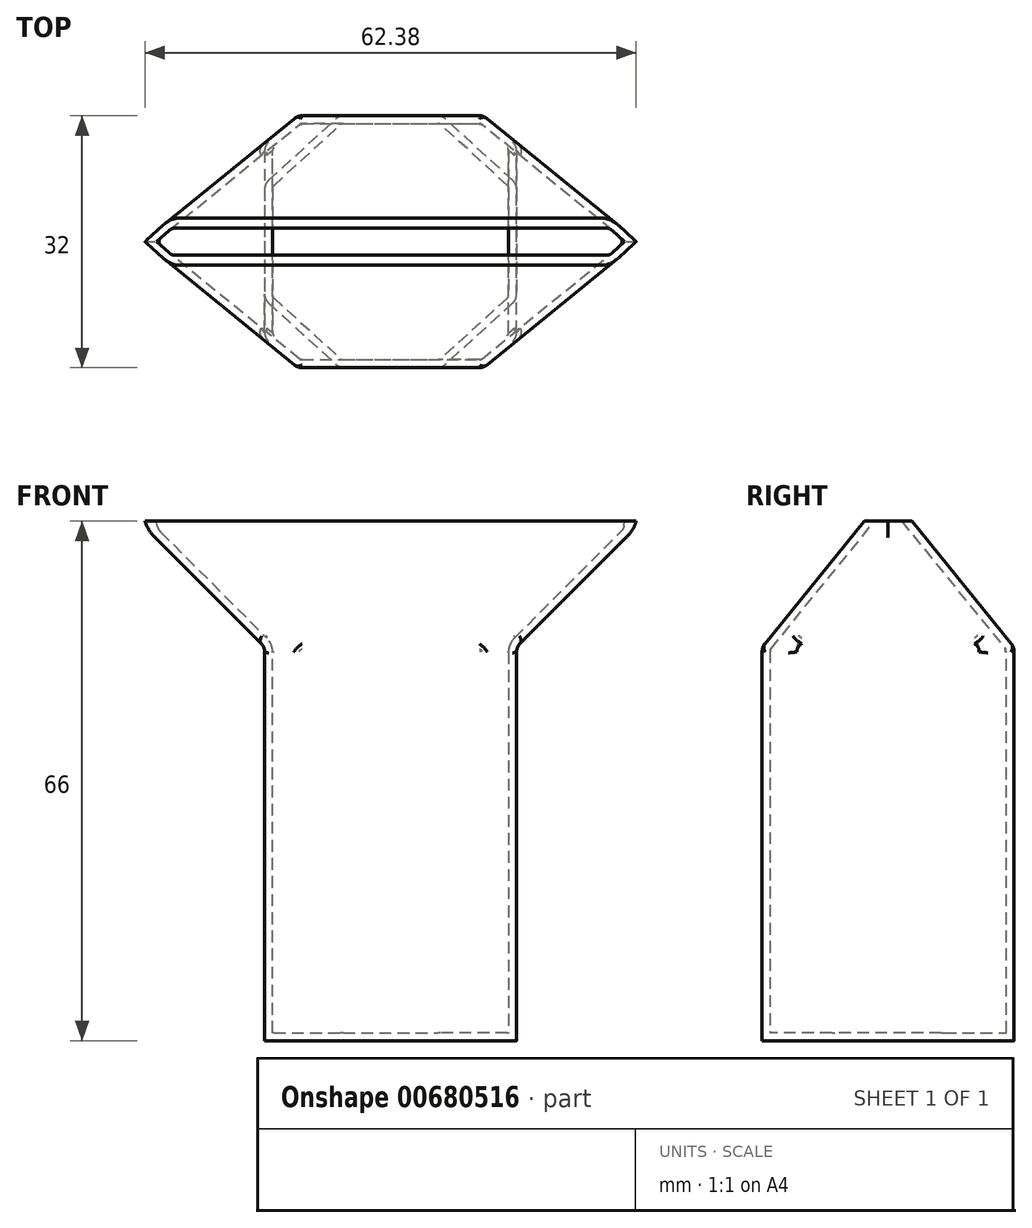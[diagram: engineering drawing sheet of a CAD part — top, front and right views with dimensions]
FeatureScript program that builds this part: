
annotation { "Feature Type Name" : "Feature", "Feature Type Description" : "" }
export const myFeature = defineFeature(function(context is Context, id is Id, definition is map)
    precondition{}
    {
        {
            assignVariable(context, id + "F0", {"name" : "length", "anyValue" : 32});
        }
        {
            assignVariable(context, id + "F1", {"name" : "depth", "anyValue" : 50});
        }
        {
            var Q0;
            Q0=qCreatedBy(makeId("Top.planeOp"),FACE);
            var sketch = newSketch(context, id + "F2", { "sketchPlane" : qUnion([Q0])});
            skLineSegment(sketch, "E0.bottom", {"start": v(-16, 16) * mm, "end": v(16, 16) * mm});
            skLineSegment(sketch, "E0.top", {"start": v(-16, -16) * mm, "end": v(16, -16) * mm});
            skLineSegment(sketch, "E0.left", {"start": v(-16, 16) * mm, "end": v(-16, -16) * mm});
            skLineSegment(sketch, "E0.right", {"start": v(16, 16) * mm, "end": v(16, -16) * mm});
            skPoint(sketch, "E0.middle", {"position": v(0, 0) * mm});
            skSolve(sketch);
        }
        {
            var Q0;
            Q0=qSketchRegion(id+"F2",true);
            extrude(context, id + "F3", {"entities" : qUnion([Q0]), "depth" : (getVariable(context, 'depth')) * mm, "offsetDistance" : 25 * mm});
        }
        {
            var Q0;
            Q0=makeQuery(id+"F3.opExtrude","CAP_FACE",FACE,{"disambiguationData":[OSD([sQuery(id+"F2.wireOp",EDGE,"E0.bottom"),sQuery(id+"F2.wireOp",EDGE,"E0.top"),sQuery(id+"F2.wireOp",EDGE,"E0.left"),sQuery(id+"F2.wireOp",EDGE,"E0.right")])],"isStart":false});
            cPlane(context, id + "F4", {"entities" : qUnion([Q0]), "cplaneType" : CPlaneType.OFFSET, "offset" : (getVariable(context, 'length') / 2) * mm, "width" : 150 * mm, "height" : 150 * mm});
        }
        {
            var Q0;
            Q0=qCreatedBy(id+"F4.planeOp",FACE);
            var sketch = newSketch(context, id + "F5", { "sketchPlane" : qUnion([Q0])});
            skLineSegment(sketch, "E1.bottom", {"start": v(32, 3) * mm, "end": v(-32, 3) * mm});
            skLineSegment(sketch, "E1.top", {"start": v(32, -3) * mm, "end": v(-32, -3) * mm});
            skLineSegment(sketch, "E1.left", {"start": v(32, 3) * mm, "end": v(32, -3) * mm});
            skLineSegment(sketch, "E1.right", {"start": v(-32, 3) * mm, "end": v(-32, -3) * mm});
            skPoint(sketch, "E1.middle", {"position": v(0, 0) * mm});
            skSolve(sketch);
        }
        {
            var Q1;
            Q1=makeQuery(id+"F3.opExtrude","CAP_FACE",FACE,{"disambiguationData":[OSD([sQuery(id+"F2.wireOp",EDGE,"E0.bottom"),sQuery(id+"F2.wireOp",EDGE,"E0.top"),sQuery(id+"F2.wireOp",EDGE,"E0.left"),sQuery(id+"F2.wireOp",EDGE,"E0.right")])],"isStart":false});
            var Q2;
            Q2=makeQuery(id+"F5.imprint","IMPRINT",FACE,{"disambiguationData":[TD([[makeQuery(id+"F5.imprint","IMPRINT",EDGE,{"derivedFrom":sQuery(id+"F5.wireOp",EDGE,"E1.bottom")}),1.0]])]});
            loft(context, id + "F6", {"operationType" : NewBodyOperationType.ADD, "sheetProfilesArray" : [{ "sheetProfileEntities" : qUnion([Q1]) }, { "sheetProfileEntities" : qUnion([Q2]) }]});
        }
        {
            var Q0;
            Q0=makeQuery(id+"F6.opLoft","SWEPT_EDGE",EDGE,{"disambiguationData":[OSD([sQuery(id+"F2.wireOp",EDGE,"E0.top"),sQuery(id+"F2.wireOp",EDGE,"E0.left"),sQuery(id+"F5.wireOp",EDGE,"E1.top"),sQuery(id+"F5.wireOp",EDGE,"E1.right")])]});
            var Q1;
            Q1=makeQuery(id+"F6.opLoft","SWEPT_EDGE",EDGE,{"disambiguationData":[OSD([sQuery(id+"F2.wireOp",EDGE,"E0.bottom"),sQuery(id+"F2.wireOp",EDGE,"E0.left"),sQuery(id+"F5.wireOp",EDGE,"E1.bottom"),sQuery(id+"F5.wireOp",EDGE,"E1.right")])]});
            var Q2;
            Q2=makeQuery(id+"F6.opLoft","SWEPT_EDGE",EDGE,{"disambiguationData":[OSD([sQuery(id+"F2.wireOp",EDGE,"E0.top"),sQuery(id+"F2.wireOp",EDGE,"E0.right"),sQuery(id+"F5.wireOp",EDGE,"E1.top"),sQuery(id+"F5.wireOp",EDGE,"E1.left")])]});
            var Q3;
            Q3=makeQuery(id+"F6.opLoft","SWEPT_EDGE",EDGE,{"disambiguationData":[OSD([sQuery(id+"F2.wireOp",EDGE,"E0.bottom"),sQuery(id+"F2.wireOp",EDGE,"E0.right"),sQuery(id+"F5.wireOp",EDGE,"E1.bottom"),sQuery(id+"F5.wireOp",EDGE,"E1.left")])]});
            chamfer(context, id + "F7", {"entities" : qUnion([Q0, Q1, Q2, Q3]), "width" : 2 * mm, "tangentPropagation" : true});
        }
        {
            var Q0;
            {var subQ0=sQuery(id+"F2.wireOp",EDGE,"E0.top");Q0=makeQuery(id+"F7.opChamfer","BLEND_EDGE",EDGE,{"blendedFrom":[makeQuery(id+"F6.opLoft","SWEPT_EDGE",EDGE,{"disambiguationData":[OSD([subQ0,sQuery(id+"F2.wireOp",EDGE,"E0.left"),sQuery(id+"F5.wireOp",EDGE,"E1.top"),sQuery(id+"F5.wireOp",EDGE,"E1.right")])]}),makeQuery(id+"F3.opExtrude","SWEPT_FACE",FACE,{"disambiguationData":[OSD([subQ0])]})],"blendedInto":[makeQuery(id+"F3.opExtrude","SWEPT_FACE",FACE,{"disambiguationData":[OSD([subQ0])]})]});}
            var Q1;
            {var subQ0=sQuery(id+"F2.wireOp",EDGE,"E0.left");Q1=makeQuery(id+"F7.opChamfer","BLEND_EDGE",EDGE,{"blendedFrom":[makeQuery(id+"F6.opLoft","SWEPT_EDGE",EDGE,{"disambiguationData":[OSD([sQuery(id+"F2.wireOp",EDGE,"E0.top"),subQ0,sQuery(id+"F5.wireOp",EDGE,"E1.top"),sQuery(id+"F5.wireOp",EDGE,"E1.right")])]}),makeQuery(id+"F3.opExtrude","SWEPT_FACE",FACE,{"disambiguationData":[OSD([subQ0])]})],"blendedInto":[makeQuery(id+"F3.opExtrude","SWEPT_FACE",FACE,{"disambiguationData":[OSD([subQ0])]})]});}
            var Q2;
            {var subQ0=sQuery(id+"F5.wireOp",EDGE,"E1.right");var subQ1=sQuery(id+"F5.wireOp",EDGE,"E1.top");var subQ2=sQuery(id+"F2.wireOp",EDGE,"E0.left");var subQ3=sQuery(id+"F2.wireOp",EDGE,"E0.top");Q2=makeQuery(id+"F7.opChamfer","BLEND_EDGE",EDGE,{"blendedFrom":[makeQuery(id+"F6.opLoft","SWEPT_EDGE",EDGE,{"disambiguationData":[OSD([subQ3,subQ2,subQ1,subQ0])]}),makeQuery(id+"F6.opLoft","SWEPT_FACE",FACE,{"disambiguationData":[OSD([sQuery(id+"F2.wireOp",EDGE,"E0.bottom"),subQ3,subQ2,sQuery(id+"F5.wireOp",EDGE,"E1.bottom"),subQ1,subQ0])]})],"blendedInto":[makeQuery(id+"F6.opLoft","SWEPT_FACE",FACE,{"disambiguationData":[OSD([sQuery(id+"F2.wireOp",EDGE,"E0.bottom"),subQ3,subQ2,sQuery(id+"F5.wireOp",EDGE,"E1.bottom"),subQ1,subQ0])]})]});}
            var Q3;
            {var subQ0=sQuery(id+"F5.wireOp",EDGE,"E1.right");var subQ1=sQuery(id+"F5.wireOp",EDGE,"E1.top");var subQ2=sQuery(id+"F2.wireOp",EDGE,"E0.left");var subQ3=sQuery(id+"F2.wireOp",EDGE,"E0.top");Q3=makeQuery(id+"F7.opChamfer","BLEND_EDGE",EDGE,{"blendedFrom":[makeQuery(id+"F6.opLoft","SWEPT_EDGE",EDGE,{"disambiguationData":[OSD([subQ3,subQ2,subQ1,subQ0])]}),makeQuery(id+"F6.opLoft","SWEPT_FACE",FACE,{"disambiguationData":[OSD([subQ3,subQ2,sQuery(id+"F2.wireOp",EDGE,"E0.right"),subQ1,sQuery(id+"F5.wireOp",EDGE,"E1.left"),subQ0])]})],"blendedInto":[makeQuery(id+"F6.opLoft","SWEPT_FACE",FACE,{"disambiguationData":[OSD([subQ3,subQ2,sQuery(id+"F2.wireOp",EDGE,"E0.right"),subQ1,sQuery(id+"F5.wireOp",EDGE,"E1.left"),subQ0])]})]});}
            var Q4;
            {var subQ0=sQuery(id+"F5.wireOp",EDGE,"E1.right");var subQ1=sQuery(id+"F5.wireOp",EDGE,"E1.bottom");var subQ2=sQuery(id+"F2.wireOp",EDGE,"E0.left");var subQ3=sQuery(id+"F2.wireOp",EDGE,"E0.bottom");Q4=makeQuery(id+"F7.opChamfer","BLEND_EDGE",EDGE,{"blendedFrom":[makeQuery(id+"F6.opLoft","SWEPT_EDGE",EDGE,{"disambiguationData":[OSD([subQ3,subQ2,subQ1,subQ0])]}),makeQuery(id+"F6.opLoft","SWEPT_FACE",FACE,{"disambiguationData":[OSD([subQ3,sQuery(id+"F2.wireOp",EDGE,"E0.top"),subQ2,subQ1,sQuery(id+"F5.wireOp",EDGE,"E1.top"),subQ0])]})],"blendedInto":[makeQuery(id+"F6.opLoft","SWEPT_FACE",FACE,{"disambiguationData":[OSD([subQ3,sQuery(id+"F2.wireOp",EDGE,"E0.top"),subQ2,subQ1,sQuery(id+"F5.wireOp",EDGE,"E1.top"),subQ0])]})]});}
            var Q5;
            {var subQ0=sQuery(id+"F2.wireOp",EDGE,"E0.left");Q5=makeQuery(id+"F7.opChamfer","BLEND_EDGE",EDGE,{"blendedFrom":[makeQuery(id+"F6.opLoft","SWEPT_EDGE",EDGE,{"disambiguationData":[OSD([sQuery(id+"F2.wireOp",EDGE,"E0.bottom"),subQ0,sQuery(id+"F5.wireOp",EDGE,"E1.bottom"),sQuery(id+"F5.wireOp",EDGE,"E1.right")])]}),makeQuery(id+"F3.opExtrude","SWEPT_FACE",FACE,{"disambiguationData":[OSD([subQ0])]})],"blendedInto":[makeQuery(id+"F3.opExtrude","SWEPT_FACE",FACE,{"disambiguationData":[OSD([subQ0])]})]});}
            var Q6;
            {var subQ0=sQuery(id+"F2.wireOp",EDGE,"E0.bottom");Q6=makeQuery(id+"F7.opChamfer","BLEND_EDGE",EDGE,{"blendedFrom":[makeQuery(id+"F6.opLoft","SWEPT_EDGE",EDGE,{"disambiguationData":[OSD([subQ0,sQuery(id+"F2.wireOp",EDGE,"E0.left"),sQuery(id+"F5.wireOp",EDGE,"E1.bottom"),sQuery(id+"F5.wireOp",EDGE,"E1.right")])]}),makeQuery(id+"F3.opExtrude","SWEPT_FACE",FACE,{"disambiguationData":[OSD([subQ0])]})],"blendedInto":[makeQuery(id+"F3.opExtrude","SWEPT_FACE",FACE,{"disambiguationData":[OSD([subQ0])]})]});}
            var Q7;
            {var subQ0=sQuery(id+"F5.wireOp",EDGE,"E1.right");var subQ1=sQuery(id+"F5.wireOp",EDGE,"E1.bottom");var subQ2=sQuery(id+"F2.wireOp",EDGE,"E0.left");var subQ3=sQuery(id+"F2.wireOp",EDGE,"E0.bottom");Q7=makeQuery(id+"F7.opChamfer","BLEND_EDGE",EDGE,{"blendedFrom":[makeQuery(id+"F6.opLoft","SWEPT_EDGE",EDGE,{"disambiguationData":[OSD([subQ3,subQ2,subQ1,subQ0])]}),makeQuery(id+"F6.opLoft","SWEPT_FACE",FACE,{"disambiguationData":[OSD([subQ3,subQ2,sQuery(id+"F2.wireOp",EDGE,"E0.right"),subQ1,sQuery(id+"F5.wireOp",EDGE,"E1.left"),subQ0])]})],"blendedInto":[makeQuery(id+"F6.opLoft","SWEPT_FACE",FACE,{"disambiguationData":[OSD([subQ3,subQ2,sQuery(id+"F2.wireOp",EDGE,"E0.right"),subQ1,sQuery(id+"F5.wireOp",EDGE,"E1.left"),subQ0])]})]});}
            var Q8;
            {var subQ0=sQuery(id+"F2.wireOp",EDGE,"E0.bottom");Q8=makeQuery(id+"F7.opChamfer","BLEND_EDGE",EDGE,{"blendedFrom":[makeQuery(id+"F6.opLoft","SWEPT_EDGE",EDGE,{"disambiguationData":[OSD([subQ0,sQuery(id+"F2.wireOp",EDGE,"E0.right"),sQuery(id+"F5.wireOp",EDGE,"E1.bottom"),sQuery(id+"F5.wireOp",EDGE,"E1.left")])]}),makeQuery(id+"F3.opExtrude","SWEPT_FACE",FACE,{"disambiguationData":[OSD([subQ0])]})],"blendedInto":[makeQuery(id+"F3.opExtrude","SWEPT_FACE",FACE,{"disambiguationData":[OSD([subQ0])]})]});}
            var Q9;
            {var subQ0=sQuery(id+"F5.wireOp",EDGE,"E1.left");var subQ1=sQuery(id+"F5.wireOp",EDGE,"E1.bottom");var subQ2=sQuery(id+"F2.wireOp",EDGE,"E0.right");var subQ3=sQuery(id+"F2.wireOp",EDGE,"E0.bottom");Q9=makeQuery(id+"F7.opChamfer","BLEND_EDGE",EDGE,{"blendedFrom":[makeQuery(id+"F6.opLoft","SWEPT_EDGE",EDGE,{"disambiguationData":[OSD([subQ3,subQ2,subQ1,subQ0])]}),makeQuery(id+"F6.opLoft","SWEPT_FACE",FACE,{"disambiguationData":[OSD([subQ3,sQuery(id+"F2.wireOp",EDGE,"E0.left"),subQ2,subQ1,subQ0,sQuery(id+"F5.wireOp",EDGE,"E1.right")])]})],"blendedInto":[makeQuery(id+"F6.opLoft","SWEPT_FACE",FACE,{"disambiguationData":[OSD([subQ3,sQuery(id+"F2.wireOp",EDGE,"E0.left"),subQ2,subQ1,subQ0,sQuery(id+"F5.wireOp",EDGE,"E1.right")])]})]});}
            var Q10;
            {var subQ0=sQuery(id+"F5.wireOp",EDGE,"E1.left");var subQ1=sQuery(id+"F5.wireOp",EDGE,"E1.bottom");var subQ2=sQuery(id+"F2.wireOp",EDGE,"E0.right");var subQ3=sQuery(id+"F2.wireOp",EDGE,"E0.bottom");Q10=makeQuery(id+"F7.opChamfer","BLEND_EDGE",EDGE,{"blendedFrom":[makeQuery(id+"F6.opLoft","SWEPT_EDGE",EDGE,{"disambiguationData":[OSD([subQ3,subQ2,subQ1,subQ0])]}),makeQuery(id+"F6.opLoft","SWEPT_FACE",FACE,{"disambiguationData":[OSD([subQ3,sQuery(id+"F2.wireOp",EDGE,"E0.top"),subQ2,subQ1,sQuery(id+"F5.wireOp",EDGE,"E1.top"),subQ0])]})],"blendedInto":[makeQuery(id+"F6.opLoft","SWEPT_FACE",FACE,{"disambiguationData":[OSD([subQ3,sQuery(id+"F2.wireOp",EDGE,"E0.top"),subQ2,subQ1,sQuery(id+"F5.wireOp",EDGE,"E1.top"),subQ0])]})]});}
            var Q11;
            {var subQ0=sQuery(id+"F2.wireOp",EDGE,"E0.right");Q11=makeQuery(id+"F7.opChamfer","BLEND_EDGE",EDGE,{"blendedFrom":[makeQuery(id+"F6.opLoft","SWEPT_EDGE",EDGE,{"disambiguationData":[OSD([sQuery(id+"F2.wireOp",EDGE,"E0.bottom"),subQ0,sQuery(id+"F5.wireOp",EDGE,"E1.bottom"),sQuery(id+"F5.wireOp",EDGE,"E1.left")])]}),makeQuery(id+"F3.opExtrude","SWEPT_FACE",FACE,{"disambiguationData":[OSD([subQ0])]})],"blendedInto":[makeQuery(id+"F3.opExtrude","SWEPT_FACE",FACE,{"disambiguationData":[OSD([subQ0])]})]});}
            var Q12;
            {var subQ0=sQuery(id+"F2.wireOp",EDGE,"E0.right");Q12=makeQuery(id+"F7.opChamfer","BLEND_EDGE",EDGE,{"blendedFrom":[makeQuery(id+"F6.opLoft","SWEPT_EDGE",EDGE,{"disambiguationData":[OSD([sQuery(id+"F2.wireOp",EDGE,"E0.top"),subQ0,sQuery(id+"F5.wireOp",EDGE,"E1.top"),sQuery(id+"F5.wireOp",EDGE,"E1.left")])]}),makeQuery(id+"F3.opExtrude","SWEPT_FACE",FACE,{"disambiguationData":[OSD([subQ0])]})],"blendedInto":[makeQuery(id+"F3.opExtrude","SWEPT_FACE",FACE,{"disambiguationData":[OSD([subQ0])]})]});}
            var Q13;
            {var subQ0=sQuery(id+"F5.wireOp",EDGE,"E1.left");var subQ1=sQuery(id+"F5.wireOp",EDGE,"E1.top");var subQ2=sQuery(id+"F2.wireOp",EDGE,"E0.right");var subQ3=sQuery(id+"F2.wireOp",EDGE,"E0.top");Q13=makeQuery(id+"F7.opChamfer","BLEND_EDGE",EDGE,{"blendedFrom":[makeQuery(id+"F6.opLoft","SWEPT_EDGE",EDGE,{"disambiguationData":[OSD([subQ3,subQ2,subQ1,subQ0])]}),makeQuery(id+"F6.opLoft","SWEPT_FACE",FACE,{"disambiguationData":[OSD([sQuery(id+"F2.wireOp",EDGE,"E0.bottom"),subQ3,subQ2,sQuery(id+"F5.wireOp",EDGE,"E1.bottom"),subQ1,subQ0])]})],"blendedInto":[makeQuery(id+"F6.opLoft","SWEPT_FACE",FACE,{"disambiguationData":[OSD([sQuery(id+"F2.wireOp",EDGE,"E0.bottom"),subQ3,subQ2,sQuery(id+"F5.wireOp",EDGE,"E1.bottom"),subQ1,subQ0])]})]});}
            var Q14;
            {var subQ0=sQuery(id+"F5.wireOp",EDGE,"E1.left");var subQ1=sQuery(id+"F5.wireOp",EDGE,"E1.top");var subQ2=sQuery(id+"F2.wireOp",EDGE,"E0.right");var subQ3=sQuery(id+"F2.wireOp",EDGE,"E0.top");Q14=makeQuery(id+"F7.opChamfer","BLEND_EDGE",EDGE,{"blendedFrom":[makeQuery(id+"F6.opLoft","SWEPT_EDGE",EDGE,{"disambiguationData":[OSD([subQ3,subQ2,subQ1,subQ0])]}),makeQuery(id+"F6.opLoft","SWEPT_FACE",FACE,{"disambiguationData":[OSD([subQ3,sQuery(id+"F2.wireOp",EDGE,"E0.left"),subQ2,subQ1,subQ0,sQuery(id+"F5.wireOp",EDGE,"E1.right")])]})],"blendedInto":[makeQuery(id+"F6.opLoft","SWEPT_FACE",FACE,{"disambiguationData":[OSD([subQ3,sQuery(id+"F2.wireOp",EDGE,"E0.left"),subQ2,subQ1,subQ0,sQuery(id+"F5.wireOp",EDGE,"E1.right")])]})]});}
            var Q15;
            {var subQ0=sQuery(id+"F2.wireOp",EDGE,"E0.top");Q15=makeQuery(id+"F7.opChamfer","BLEND_EDGE",EDGE,{"blendedFrom":[makeQuery(id+"F6.opLoft","SWEPT_EDGE",EDGE,{"disambiguationData":[OSD([subQ0,sQuery(id+"F2.wireOp",EDGE,"E0.right"),sQuery(id+"F5.wireOp",EDGE,"E1.top"),sQuery(id+"F5.wireOp",EDGE,"E1.left")])]}),makeQuery(id+"F3.opExtrude","SWEPT_FACE",FACE,{"disambiguationData":[OSD([subQ0])]})],"blendedInto":[makeQuery(id+"F3.opExtrude","SWEPT_FACE",FACE,{"disambiguationData":[OSD([subQ0])]})]});}
            var Q16;
            {var subQ0=sQuery(id+"F2.wireOp",EDGE,"E0.right");Q16=makeQuery(id+"F6.boolean.opBoolean","MERGE",EDGE,{"derivedFrom":[makeQuery(id+"F3.opExtrude","CAP_EDGE",EDGE,{"disambiguationData":[OSD([subQ0])],"isStart":false}),makeQuery(id+"F6.opLoft","MID_CAP_EDGE",EDGE,{"disambiguationData":[OSD([sQuery(id+"F2.wireOp",EDGE,"E0.bottom"),sQuery(id+"F2.wireOp",EDGE,"E0.top"),subQ0])],"capPos":0.0})]});}
            var Q17;
            {var subQ0=sQuery(id+"F2.wireOp",EDGE,"E0.left");Q17=makeQuery(id+"F6.boolean.opBoolean","MERGE",EDGE,{"derivedFrom":[makeQuery(id+"F3.opExtrude","CAP_EDGE",EDGE,{"disambiguationData":[OSD([subQ0])],"isStart":false}),makeQuery(id+"F6.opLoft","MID_CAP_EDGE",EDGE,{"disambiguationData":[OSD([sQuery(id+"F2.wireOp",EDGE,"E0.bottom"),sQuery(id+"F2.wireOp",EDGE,"E0.top"),subQ0])],"capPos":0.0})]});}
            var Q18;
            {var subQ0=sQuery(id+"F2.wireOp",EDGE,"E0.top");Q18=makeQuery(id+"F6.boolean.opBoolean","MERGE",EDGE,{"derivedFrom":[makeQuery(id+"F3.opExtrude","CAP_EDGE",EDGE,{"disambiguationData":[OSD([subQ0])],"isStart":false}),makeQuery(id+"F6.opLoft","MID_CAP_EDGE",EDGE,{"disambiguationData":[OSD([subQ0,sQuery(id+"F2.wireOp",EDGE,"E0.left"),sQuery(id+"F2.wireOp",EDGE,"E0.right")])],"capPos":0.0})]});}
            var Q19;
            {var subQ0=sQuery(id+"F2.wireOp",EDGE,"E0.bottom");Q19=makeQuery(id+"F6.boolean.opBoolean","MERGE",EDGE,{"derivedFrom":[makeQuery(id+"F3.opExtrude","CAP_EDGE",EDGE,{"disambiguationData":[OSD([subQ0])],"isStart":false}),makeQuery(id+"F6.opLoft","MID_CAP_EDGE",EDGE,{"disambiguationData":[OSD([subQ0,sQuery(id+"F2.wireOp",EDGE,"E0.left"),sQuery(id+"F2.wireOp",EDGE,"E0.right")])],"capPos":0.0})]});}
            fillet(context, id + "F8", {"entities" : qUnion([Q0, Q1, Q2, Q3, Q4, Q5, Q6, Q7, Q8, Q9, Q10, Q11, Q12, Q13, Q14, Q15, Q16, Q17, Q18, Q19]), "radius" : 1.5 * mm, "tangentPropagation" : true, "allowEdgeOverflow" : false});
        }
        {
            var Q0;
            Q0=makeQuery(id+"F6.opLoft","CAP_FACE",FACE,{"disambiguationData":[OSD([makeQuery(id+"F5.imprint","IMPRINT",FACE,{"disambiguationData":[TD([[makeQuery(id+"F5.imprint","IMPRINT",EDGE,{"derivedFrom":sQuery(id+"F5.wireOp",EDGE,"E1.bottom")}),1.0]])]})])],"isStart":true});
            shell(context, id + "F9", {"entities" : qUnion([Q0]), "thickness" : 1 * mm});
        }
    });
